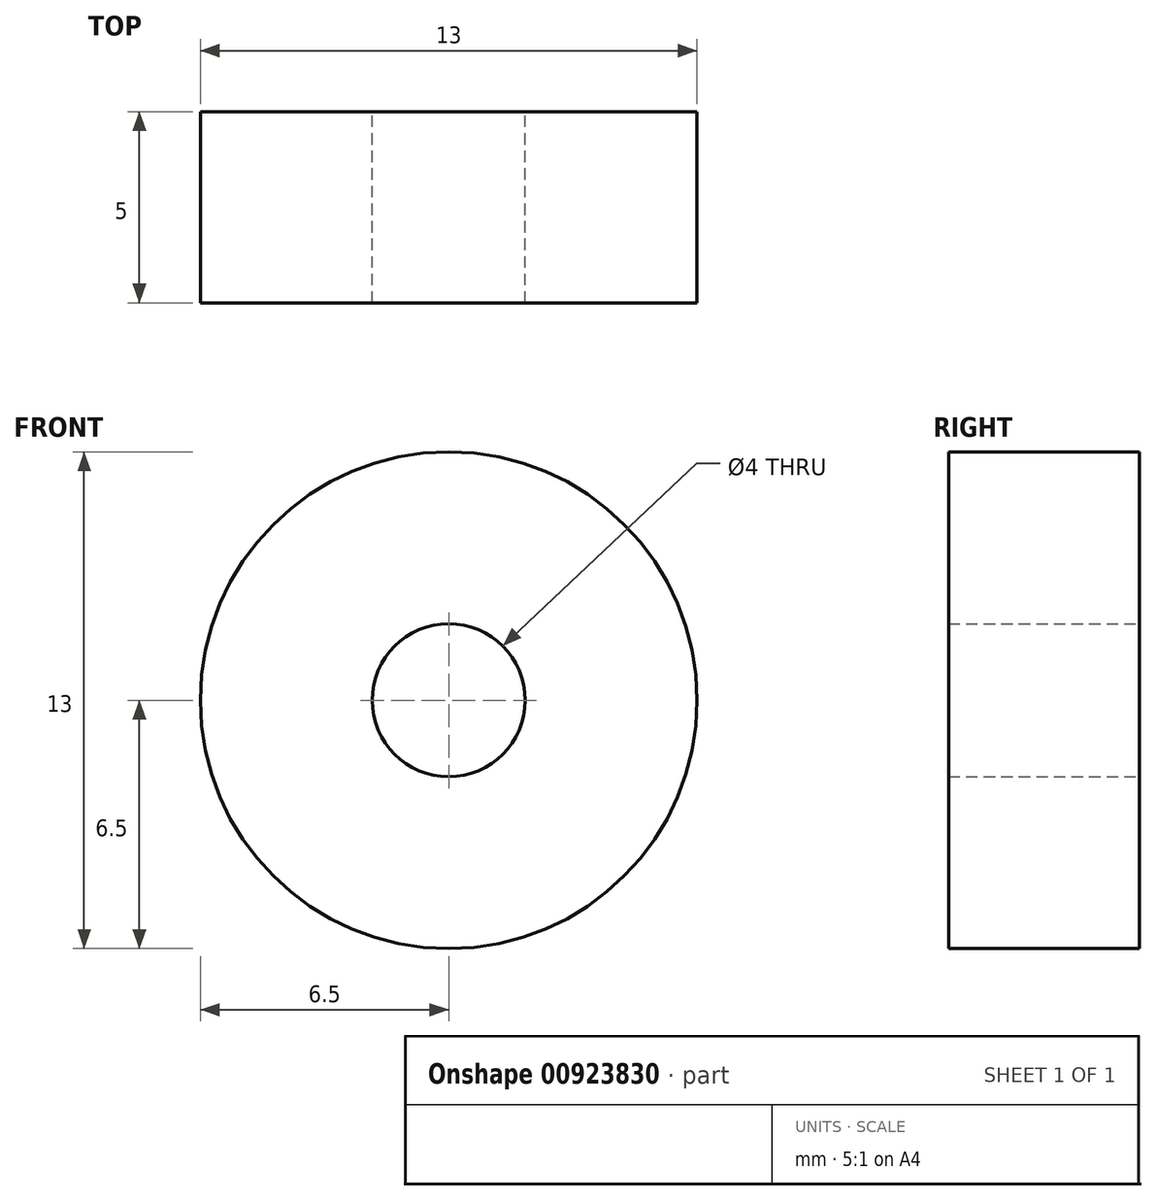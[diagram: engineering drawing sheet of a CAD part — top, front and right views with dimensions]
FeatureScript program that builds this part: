
annotation { "Feature Type Name" : "Feature", "Feature Type Description" : "" }
export const myFeature = defineFeature(function(context is Context, id is Id, definition is map)
    precondition{}
    {
        {
            var Q0;
            Q0=qCreatedBy(makeId("Front.planeOp"),FACE);
            var sketch = newSketch(context, id + "F0", { "sketchPlane" : qUnion([Q0])});
            skCircle(sketch, "E0", {"center": v(0, 0) * mm, "radius": 2 * mm});
            skCircle(sketch, "E1", {"center": v(0, 0) * mm, "radius": 6.5 * mm});
            skSolve(sketch);
        }
        {
            var Q0;
            Q0=makeQuery(id+"F0.imprint","IMPRINT",FACE,{"disambiguationData":[TD([[makeQuery(id+"F0.imprint","IMPRINT",EDGE,{"derivedFrom":sQuery(id+"F0.wireOp",EDGE,"E0")}),-1.0]])]});
            extrude(context, id + "F1", {"entities" : qUnion([Q0]), "depth" : 5 * mm, "offsetDistance" : 25 * mm});
        }
    });
